# Revit family: Вентилятор круглый V Compact металл
name_source: partatom
category: Оборудование
units: mm (PartAtom-declared; Revit-internal decimal feet)

## family parameters
Всегда вертикально = Да
Заголовок OmniClass = Climate Control (HVAC)
На основе рабочей плоскости = Нет
Номер OmniClass = 23.75.00.00
Общий = Нет
При загрузке вырезать с полостями = Нет
Размер круглого соединителя = Использовать диаметр
Тип детали = Нормальный
Точка расчета площади = Нет

## types (6) — shared parameters
ADSK_Единица измерения = шт.
ADSK_Завод-изготовитель = Naveka
ADSK_Наименование = Вентилятор для круглого канала
ADSK_Примечание = https://progress-nw.ru
Материал = RAL 0000 Серый металл
Напряжение U,В = 1-220

## per-type parameters (varying)
| type | ADSK_Марка | ADSK_Масса_Текст | B | D | D+0.5 | D+4.5 | H | L | d | Мощность двигателя N,Вт | Сила тока J, А | Частота вращения n, об/мин |
| V-100 | V-100 Compact | 4.3 кг | 250 мм | 49 мм | 50 мм | 54 мм | 134 мм | 360 мм | 100 мм | 52 | 0.23 | 2350 |
| V-125 | V-125 Compact | 4.8 кг | 290 мм | 62 мм | 62 мм | 66 мм | 134 мм | 360 мм | 125 мм | 52 | 0.23 | 2350 |
| V-160 | V-160 Compact | 6.2 кг | 320 мм | 79 мм | 80 мм | 84 мм | 169 мм | 400 мм | 160 мм | 85 | 0.38 | 2700 |
| V-200 | V-200 Compact | 7.7 кг | 350 мм | 99 мм | 100 мм | 104 мм | 213 мм | 400 мм | 200 мм | 135 | 0.6 | 2650 |
| V-250 | V-250 Compact | 10.1 кг | 400 мм | 124 мм | 125 мм | 129 мм | 259 мм | 450 мм | 250 мм | 210 | 0.93 | 2500 |
| V-315 | V-315 Compact | 12.8 кг | 450 мм | 157 мм | 157 мм | 161 мм | 309 мм | 500 мм | 315 мм | 225 | 1.0 | 2700 |
